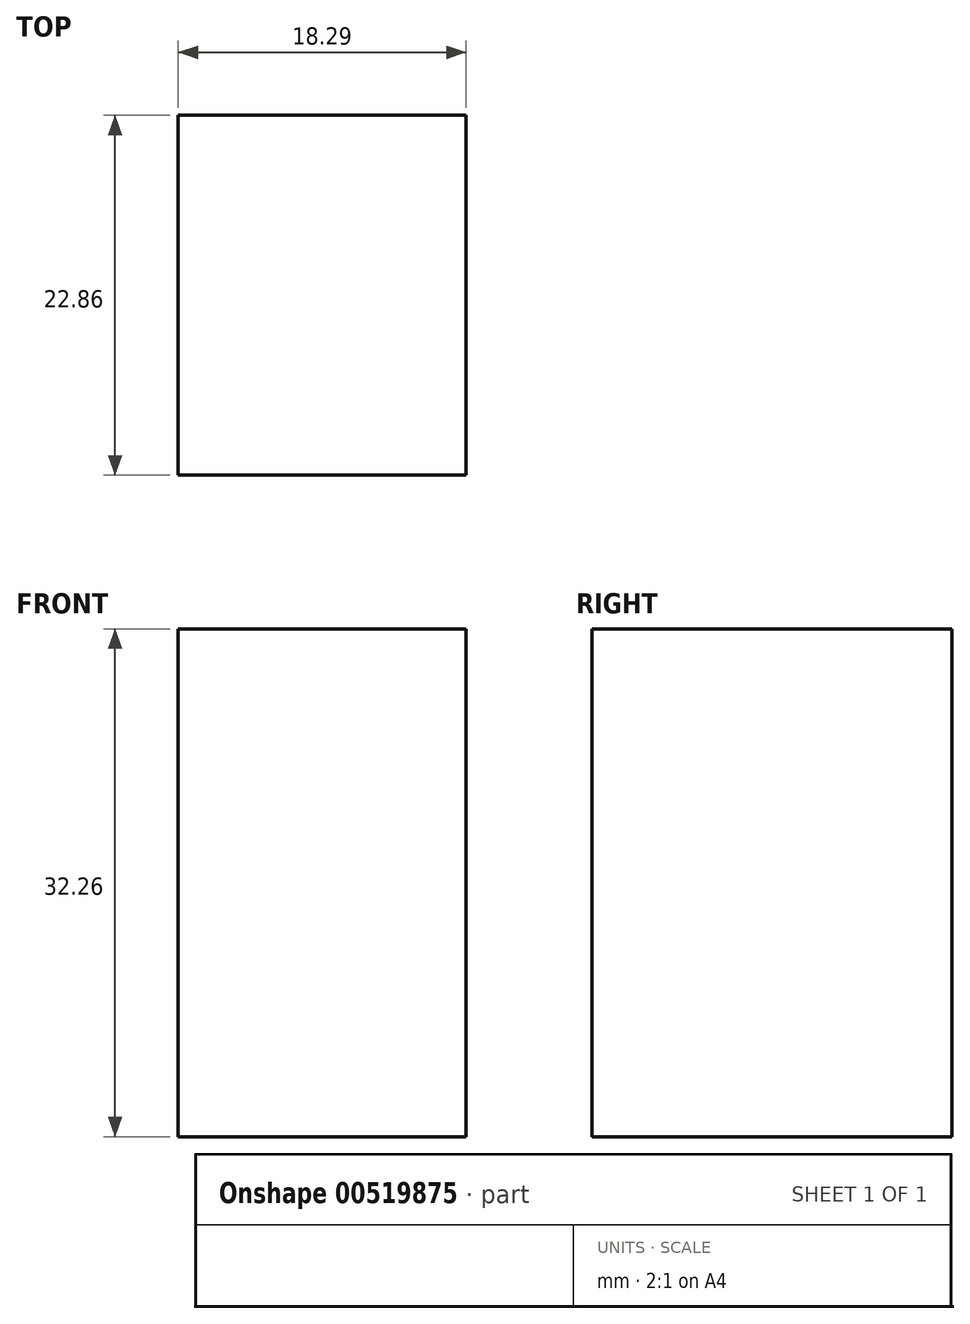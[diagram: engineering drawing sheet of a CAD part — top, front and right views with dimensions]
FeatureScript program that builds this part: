
annotation { "Feature Type Name" : "Feature", "Feature Type Description" : "" }
export const myFeature = defineFeature(function(context is Context, id is Id, definition is map)
    precondition{}
    {
        {
            var Q0;
            Q0=qCreatedBy(makeId("Front.planeOp"),FACE);
            var sketch = newSketch(context, id + "F0", { "sketchPlane" : qUnion([Q0])});
            skLineSegment(sketch, "E0.bottom", {"start": v(23.2, 41.45) * mm, "end": v(41.5, 41.45) * mm});
            skLineSegment(sketch, "E0.top", {"start": v(23.2, 9.2) * mm, "end": v(41.5, 9.2) * mm});
            skLineSegment(sketch, "E0.left", {"start": v(23.2, 41.45) * mm, "end": v(23.2, 9.2) * mm});
            skLineSegment(sketch, "E0.right", {"start": v(41.5, 41.45) * mm, "end": v(41.5, 9.2) * mm});
            skSolve(sketch);
        }
        {
            var Q0;
            Q0 = qSketchRegion(id + "F0", true);
            extrude(context, id + "F1", {"entities" : qUnion([Q0]), "depth" : 22.86 * mm, "offsetDistance" : 25.4 * mm});
        }
    });
